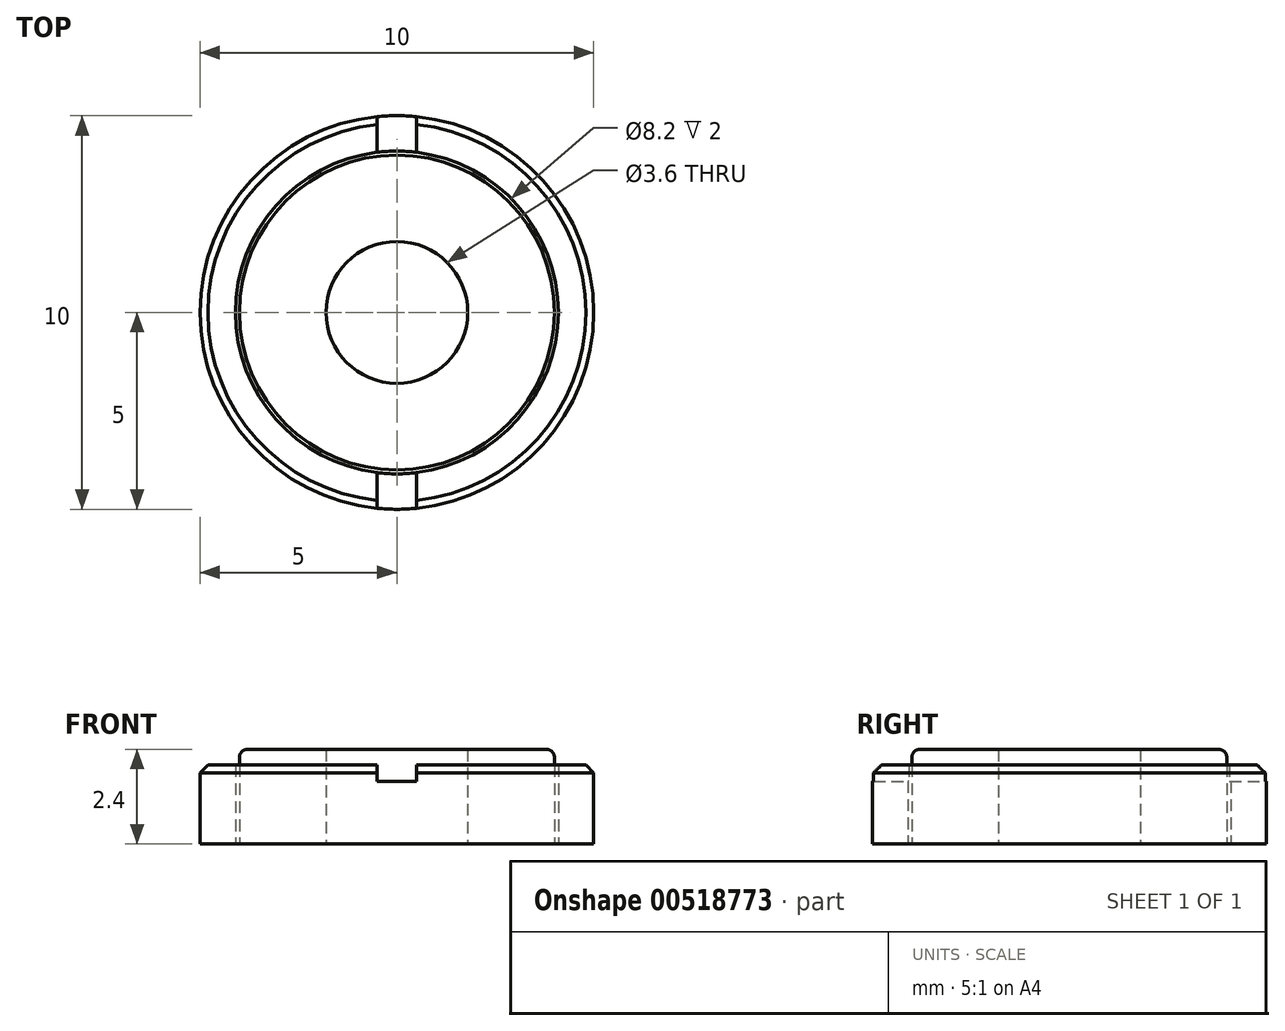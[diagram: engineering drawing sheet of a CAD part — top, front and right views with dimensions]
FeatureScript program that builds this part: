
annotation { "Feature Type Name" : "Feature", "Feature Type Description" : "" }
export const myFeature = defineFeature(function(context is Context, id is Id, definition is map)
    precondition{}
    {
        {
            var Q0;
            Q0=qCreatedBy(makeId("Top.planeOp"),FACE);
            var sketch = newSketch(context, id + "F0", { "sketchPlane" : qUnion([Q0])});
            skCircle(sketch, "E0", {"center": v(0, 0) * mm, "radius": 4 * mm});
            skCircle(sketch, "E1", {"center": v(0, 0) * mm, "radius": 4.1 * mm});
            skCircle(sketch, "E2", {"center": v(0, 0) * mm, "radius": 5 * mm});
            skSolve(sketch);
        }
        {
            var Q0;
            Q0=makeQuery(id+"F0.imprint","IMPRINT",FACE,{"disambiguationData":[TD([[makeQuery(id+"F0.imprint","IMPRINT",EDGE,{"derivedFrom":sQuery(id+"F0.wireOp",EDGE,"E0")}),1.0]])]});
            extrude(context, id + "F1", {"entities" : qUnion([Q0]), "depth" : 2.4 * mm, "offsetDistance" : 25 * mm});
        }
        {
            var Q0;
            Q0 = qSketchRegion(id + "F0", true);
            extrude(context, id + "F2", {"entities" : qUnion([Q0]), "depth" : 2 * mm, "offsetDistance" : 25 * mm});
        }
        {
            var Q0;
            Q0=sQuery(id+"F0.wireOp",VERTEX,"E0.center");
            var Q1;
            Q1=makeQuery(id+"F1.opExtrude","SWEPT_BODY",BODY,{"disambiguationData":[OSD([sQuery(id+"F0.wireOp",EDGE,"E0")])]});
            hole(context, id + "F3", {"style" : HoleStyle.SIMPLE, "endStyle" : HoleEndStyle.THROUGH, "oppositeDirection" : true, "holeDiameter" : 3.6 * mm, "isTappedThrough" : true, "tappedDepth" : 12 * mm, "tapClearance" : 3, "locations" : qUnion([Q0]), "scope" : qUnion([Q1])});
        }
        {
            var Q0;
            Q0=makeQuery(id+"F1.opExtrude","CAP_EDGE",EDGE,{"disambiguationData":[OSD([sQuery(id+"F0.wireOp",EDGE,"E0")])],"isStart":false});
            var Q1;
            Q1=makeQuery(id+"F3.hole-0.boolean.opBoolean","INTERSECT",EDGE,{"derivedFrom":[makeQuery(id+"F1.opExtrude","CAP_FACE",FACE,{"disambiguationData":[OSD([sQuery(id+"F0.wireOp",EDGE,"E0")])],"isStart":false}),makeQuery(id+"F3.hole-0.opRevolve","SWEPT_FACE",FACE,{"disambiguationData":[OSD([sQuery(id+"F3.hole-0.sketch.wireOp",EDGE,"core_line_2")])]})]});
            fillet(context, id + "F4", {"entities" : qUnion([Q0, Q1]), "radius" : 0.2 * mm, "tangentPropagation" : true, "allowEdgeOverflow" : false});
        }
        {
            var Q0;
            Q0=makeQuery(id+"F2.opExtrude","CAP_EDGE",EDGE,{"disambiguationData":[OSD([sQuery(id+"F0.wireOp",EDGE,"E2")])],"isStart":false});
            chamfer(context, id + "F5", {"entities" : qUnion([Q0]), "width" : 0.2 * mm, "tangentPropagation" : true});
        }
        {
            var Q0;
            Q0=qCreatedBy(makeId("Front.planeOp"),FACE);
            var sketch = newSketch(context, id + "F6", { "sketchPlane" : qUnion([Q0])});
            skLineSegment(sketch, "E3", {"start": v(0, 2.1) * mm, "end": v(0, 1.6) * mm});
            skLineSegment(sketch, "E4", {"start": v(0, 1.6) * mm, "end": v(1, 1.6) * mm});
            skLineSegment(sketch, "E5", {"start": v(1, 1.6) * mm, "end": v(1, 2.1) * mm});
            skLineSegment(sketch, "E6", {"start": v(1, 2.1) * mm, "end": v(0, 2.1) * mm});
            skSolve(sketch);
        }
        {
            var Q0;
            Q0 = qSketchRegion(id + "F6", true);
            extrude(context, id + "F7", {"entities" : qUnion([Q0]), "depth" : 25 * mm, "offsetDistance" : 25 * mm});
        }
        {
            var Q0;
            Q0=makeQuery(id+"F7.opExtrude","SWEPT_BODY",BODY,{"disambiguationData":[OSD([sQuery(id+"F6.wireOp",EDGE,"E3"),sQuery(id+"F6.wireOp",EDGE,"E4"),sQuery(id+"F6.wireOp",EDGE,"E5"),sQuery(id+"F6.wireOp",EDGE,"E6")])]});
            transform(context, id + "F8", {"entities" : qUnion([Q0]), "transformType" : TransformType.TRANSLATION_3D, "dx" : -0.5 * mm, "dy" : 13.3 * mm, "dz" : 0 * mm, "makeCopy" : false});
        }
        {
            var Q0;
            Q0=makeQuery(id+"F7.opExtrude","SWEPT_BODY",BODY,{"disambiguationData":[OSD([sQuery(id+"F6.wireOp",EDGE,"E3"),sQuery(id+"F6.wireOp",EDGE,"E4"),sQuery(id+"F6.wireOp",EDGE,"E5"),sQuery(id+"F6.wireOp",EDGE,"E6")])]});
            var Q1;
            Q1=makeQuery(id+"F2.opExtrude","SWEPT_BODY",BODY,{"disambiguationData":[OSD([sQuery(id+"F0.wireOp",EDGE,"E1"),sQuery(id+"F0.wireOp",EDGE,"E2")])]});
            booleanBodies(context, id + "F9", {"operationType" : BooleanOperationType.SUBTRACTION, "tools" : qUnion([Q0]), "targets" : qUnion([Q1])});
        }
    });
